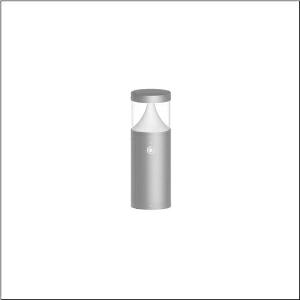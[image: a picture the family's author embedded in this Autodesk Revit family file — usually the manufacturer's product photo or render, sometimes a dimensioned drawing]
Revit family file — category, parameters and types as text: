
# Revit family: cl_31_poller_40_sensor_5cl424803
name_source: partatom
category: Lighting Fixtures
units: mm (PartAtom-declared; Revit-internal decimal feet)

## family parameters
Cut with Voids When Loaded = No
Host = Face
Light Source = No
Part Type = Normal
Room Calculation Point = No
Round Connector Dimension = Use Diameter
Shared = No

## types (1)
- --- (1 x LED, 800 lm, 7.2 W, 3000K)
    Apparent Load = 7 VA
    CIE Flux Codes = 19 66 88 92 100
    Color Rendering = 80
    Color Temperature = 3000K
    Default Elevation = 1800 mm
    Description = CL 31 Bollard 40 Sensor, bollard luminaire, primary light control with lens, of PC, primary optical cover: cover panel, of PC, transparent, secondary light control with reflector, of PC, primary light characteristic: asymmetric, LED, rated luminous flux: 800lm, luminous efficacy: 110lm/W, light colour: 830, colour temperature: 3000K, control gear: ECG DALI, with terminal, 5-pole, max. 2.5mm², mains connection: 220..240V, AC, 50/60Hz, rated input power: 7.2W, luminaire housing, of aluminium, powder-coated, Siteco® metallic grey, diameter: 170mm, height: 400mm, PIR sensor, protection rating (complete): IP65, insulation class (complete): insulation class I (protective earthing), certification: CE, ENEC, impact resistance: IK08, permissible operating ambient temperature for outdoor applications: -20..+50°C, packaging unit: 1 piece
    Height = 200 mm  [stored 0.656168 ft]
    Lamp = 1 x LED
    Lamp Light Flux = 800 lm
    Lamp Power = 7.2 W
    Lamp count = 1
    Length = 170 mm  [stored 0.557743 ft]
    Luminous efficacy = 111 lm/W
    Manufacturer = Siteco
    ModVariant = No
    Model = 5CL424803
    Mounting Place = Floor
    Mounting Type = Freestanding
    Number of Poles = 1
    OnlyDefault = Yes
    Power Factor = 1
    Product Name = CL 31 Poller 40 Sensor
    Product group = bollard luminaire
    ProductGroupID = 1304
    Protection Class = Protection class I
    Protection Degree = IP 65
    RLX_Detail_Level = 1
    RLX_Emergency_Light_Flux = 0 lm
    RLX_Emergency_Type = 0
    RLX_Emergency_Type_DB = No
    RlxData = <blob elided: 63141 chars, md5=e6d6cf11>
    Socket = socket
    Standby Power = 0 W
    System Light Flux = 800 lm
    System Power = 7 W
    Type Comments = factory setting: luminous flux: 100 % | dim-lin: 254 | 182 mA
    Type Image = l_1006905.jpg
    URL = http://relux.com
    VarID = @adj_130297
    Voltage = 0 V
    Weight = 0.00 kg
    Width = 0 mm  [stored 0 ft]

note: [stored X ft] marks values corroborated as IEEE doubles in the binary element streams (Revit-internal decimal feet)

## geometry (parser evidence)
native form markers: Blend x4, Sweep x11
no freeform markers — native parametric forms only
